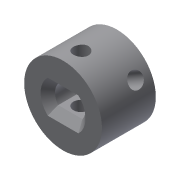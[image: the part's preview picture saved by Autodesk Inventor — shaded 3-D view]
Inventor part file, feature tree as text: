
AUTODESK INVENTOR PART (.ipt)
format: ipt  version: 2019.4 (Build 234330000, 330)  size: 177,664 bytes
history: native  units: mm
features: reference x9, other x5, sketch x4, extrude x3, projected_geometry x3, plane x1, chamfer x1, pattern_circular x1, hole x1
ambient origin geometry x8: Origin, YZ Plane, XZ Plane, XY Plane, X Axis, Y Axis, Z Axis, Center Point
bodies: Solid1 (feature_tree)
feature tree (28):
  sketch  "Sketch1"  dims[d2=4.0mm d3=0.0mm d5=5.0mm d6=0.0mm]
  plane  "Work Plane1"
  extrude  "Extrusion1"  Depth=5.0mm TaperAngle=0.0deg
  extrude  "Extrusion2"  Depth=5.4mm
  chamfer  "Chamfer1"  Distance=13.0mm
  extrude  "Extrusion3"  Depth=10.0mm
  pattern_circular  "Circular Pattern1"  [2 undecoded]
  hole  "Hole1"  [1 undecoded]
  reference  "Reference1"
  reference  "Reference2"
  reference  "Reference3"
  reference  "Reference4"
  sketch  "Sketch2"  dims[d7=1.2mm d8=2.0mm d9=45.0deg d10=5.4mm]
  reference  "Reference5"
  reference  "Reference6"
  reference  "Reference7"
  reference  "Reference8"
  reference  "Reference9"
  sketch  "Sketch3"  dims[d11=3.1mm]
  projected_geometry  "Projected Loop2"
  sketch  "Sketch4"  dims[d12=2.55mm d13=13.0mm d14=2.5mm d15=2.5mm d16=10.0mm d17=0.0mm d18=30.0mm d19=360.0deg d21=2.5mm d22=6.0mm d23=4.0mm d24=2.0mm d25=90.0deg d26=8.0mm d27=20.594885mm]
  projected_geometry  "Projected Loop3"
  projected_geometry  "Projected Loop4"
  other  "Assembly_XY_Translator_Lightsheet_v2.iam"
  other  "DIN 912 - replaced by DIN EN ISO 4762 M3 x 30:1"
  other  "ANSI B18.2.4.2M M3x0.5:2"
  other  "00_X_Translator_Lightsheet_v4:1"
  other  "28BYJ-48:1"
note: 3 required parameter values undecoded (feature->parameter linkage not recoverable at this tier; creation-order binding heuristic only, values carry confidence <= 0.55)
